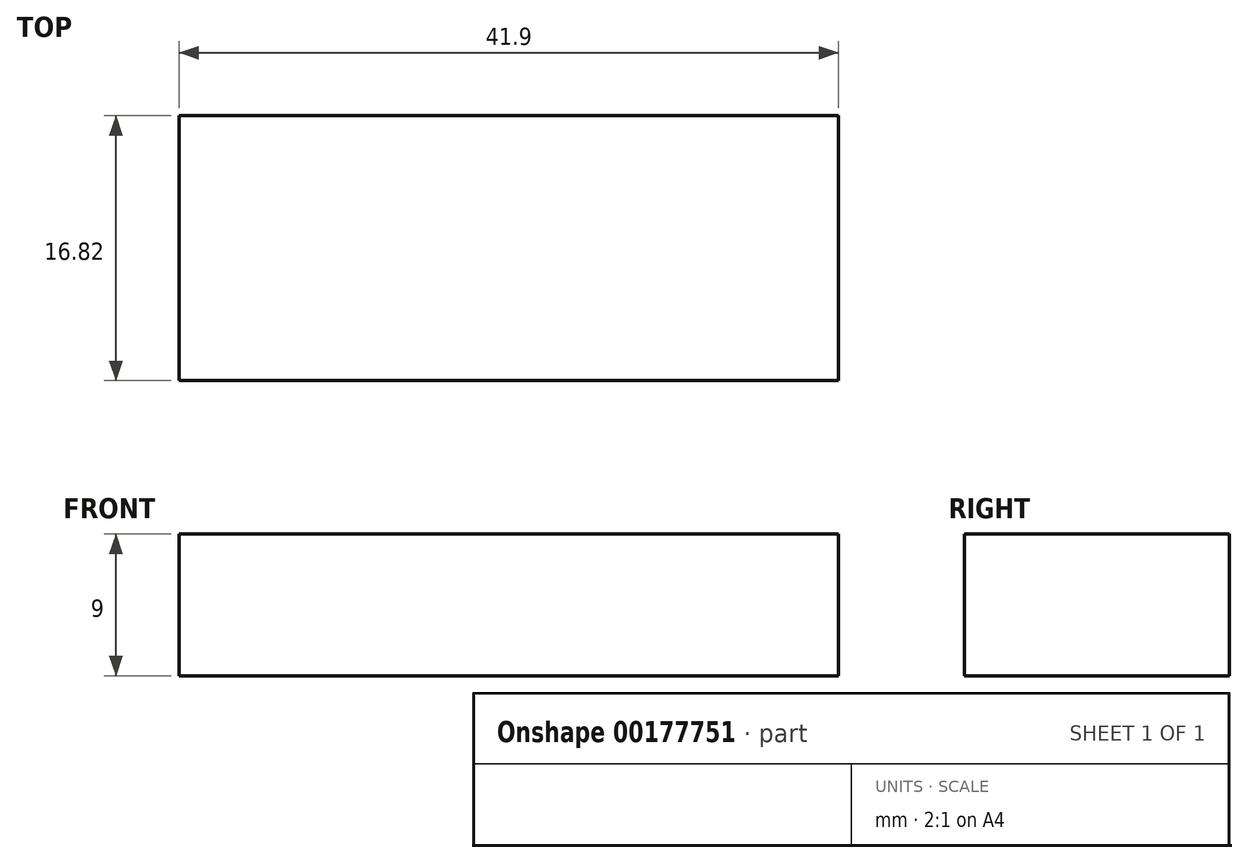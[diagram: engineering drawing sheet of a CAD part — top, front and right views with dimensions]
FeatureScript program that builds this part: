
annotation { "Feature Type Name" : "Feature", "Feature Type Description" : "" }
export const myFeature = defineFeature(function(context is Context, id is Id, definition is map)
    precondition{}
    {
        {
            var Q0;
            Q0=qCreatedBy(makeId("Top.planeOp"),FACE);
            var sketch = newSketch(context, id + "F0", { "sketchPlane" : qUnion([Q0])});
            skLineSegment(sketch, "E0.bottom", {"start": v(-0.69, -2.41) * mm, "end": v(41.21, -2.41) * mm});
            skLineSegment(sketch, "E0.top", {"start": v(-0.69, -19.23) * mm, "end": v(41.21, -19.23) * mm});
            skLineSegment(sketch, "E0.left", {"start": v(-0.69, -2.41) * mm, "end": v(-0.69, -19.23) * mm});
            skLineSegment(sketch, "E0.right", {"start": v(41.21, -2.41) * mm, "end": v(41.21, -19.23) * mm});
            skSolve(sketch);
        }
        {
            var Q0;
            Q0 = qSketchRegion(id + "F0", true);
            extrude(context, id + "F1", {"entities" : qUnion([Q0]), "depth" : 9 * mm});
        }
    });
